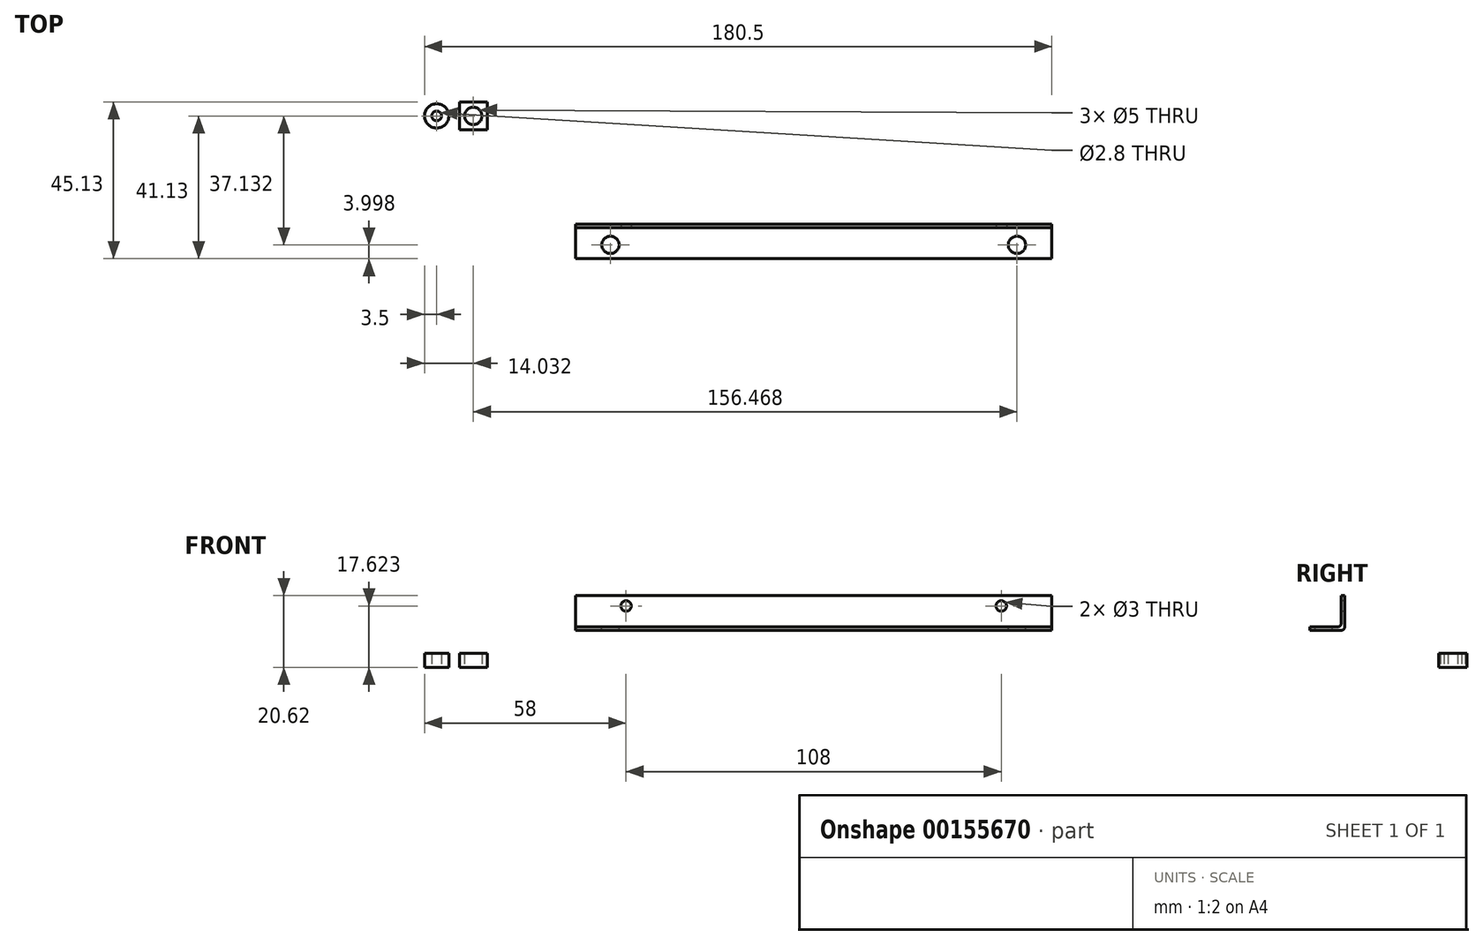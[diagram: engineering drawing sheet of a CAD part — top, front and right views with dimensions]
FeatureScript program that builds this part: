
annotation { "Feature Type Name" : "Feature", "Feature Type Description" : "" }
export const myFeature = defineFeature(function(context is Context, id is Id, definition is map)
    precondition{}
    {
        {
            var Q0;
            Q0=qCreatedBy(makeId("Right.planeOp"),FACE);
            var sketch = newSketch(context, id + "F0", { "sketchPlane" : qUnion([Q0])});
            skLineSegment(sketch, "E0.bottom", {"start": v(-31.13, 20.62) * mm, "end": v(-32.13, 20.62) * mm});
            skLineSegment(sketch, "E0.left", {"start": v(-31.13, 20.62) * mm, "end": v(-31.13, 10.62) * mm});
            skLineSegment(sketch, "E0.right", {"start": v(-32.13, 20.62) * mm, "end": v(-32.13, 11.62) * mm});
            skLineSegment(sketch, "E1.bottom", {"start": v(-31.13, 10.62) * mm, "end": v(-41.13, 10.62) * mm});
            skLineSegment(sketch, "E1.top", {"start": v(-32.13, 11.62) * mm, "end": v(-41.13, 11.62) * mm});
            skLineSegment(sketch, "E1.right", {"start": v(-41.13, 10.62) * mm, "end": v(-41.13, 11.62) * mm});
            skSolve(sketch);
        }
        {
            var Q0;
            Q0 = qSketchRegion(id + "F0", true);
            extrude(context, id + "F1", {"entities" : qUnion([Q0]), "depth" : 137 * mm});
        }
        {
            var Q0;
            Q0=makeQuery(id+"F1.opExtrude","SWEPT_FACE",FACE,{"disambiguationData":[OSD([sQuery(id+"F0.wireOp",EDGE,"E0.right")])]});
            var sketch = newSketch(context, id + "F2", { "sketchPlane" : qUnion([Q0])});
            skCircle(sketch, "E2", {"center": v(14.5, 17.62) * mm, "radius": 1.5 * mm});
            skCircle(sketch, "E3", {"center": v(122.5, 17.62) * mm, "radius": 1.5 * mm});
            skSolve(sketch);
        }
        {
            var Q0;
            Q0 = qSketchRegion(id + "F2", true);
            extrude(context, id + "F3", {"entities" : qUnion([Q0]), "operationType" : NewBodyOperationType.REMOVE, "oppositeDirection" : true, "depth" : 2 * mm});
        }
        {
            var Q0;
            Q0=makeQuery(id+"F1.opExtrude","SWEPT_FACE",FACE,{"disambiguationData":[OSD([sQuery(id+"F0.wireOp",EDGE,"E1.top")])]});
            var sketch = newSketch(context, id + "F4", { "sketchPlane" : qUnion([Q0])});
            skCircle(sketch, "E4", {"center": v(10, -37.13) * mm, "radius": 2.5 * mm});
            skCircle(sketch, "E5", {"center": v(127, -37.13) * mm, "radius": 2.5 * mm});
            skSolve(sketch);
        }
        {
            var Q0;
            Q0 = qSketchRegion(id + "F4", true);
            extrude(context, id + "F5", {"entities" : qUnion([Q0]), "operationType" : NewBodyOperationType.REMOVE, "oppositeDirection" : true, "depth" : 2 * mm});
        }
        {
            var Q0;
            Q0=makeQuery(id+"F1.opExtrude","SWEPT_EDGE",EDGE,{"disambiguationData":[OSD([sQuery(id+"F0.wireOp",EDGE,"E0.left"),sQuery(id+"F0.wireOp",EDGE,"E1.bottom")])]});
            var Q1;
            Q1=makeQuery(id+"F1.opExtrude","SWEPT_EDGE",EDGE,{"disambiguationData":[OSD([sQuery(id+"F0.wireOp",EDGE,"E0.right"),sQuery(id+"F0.wireOp",EDGE,"E1.top")])]});
            fillet(context, id + "F6", {"entities" : qUnion([Q0, Q1]), "radius" : 1 * mm, "tangentPropagation" : true, "allowEdgeOverflow" : false});
        }
        {
            var Q0;
            Q0=qCreatedBy(makeId("Top.planeOp"),FACE);
            var sketch = newSketch(context, id + "F7", { "sketchPlane" : qUnion([Q0])});
            skLineSegment(sketch, "E6.bottom", {"start": v(-25.47, -4) * mm, "end": v(-33.47, -4) * mm});
            skLineSegment(sketch, "E6.top", {"start": v(-25.47, 4) * mm, "end": v(-33.47, 4) * mm});
            skLineSegment(sketch, "E6.left", {"start": v(-25.47, -4) * mm, "end": v(-25.47, 4) * mm});
            skLineSegment(sketch, "E6.right", {"start": v(-33.47, -4) * mm, "end": v(-33.47, 4) * mm});
            skPoint(sketch, "E6.middle", {"position": v(-29.47, 0) * mm});
            skCircle(sketch, "E7", {"center": v(-29.47, 0) * mm, "radius": 2.5 * mm});
            skSolve(sketch);
        }
        {
            var Q0;
            Q0 = qSketchRegion(id + "F7", true);
            extrude(context, id + "F8", {"entities" : qUnion([Q0]), "depth" : 4 * mm});
        }
        {
            var Q0;
            Q0=qCreatedBy(makeId("Top.planeOp"),FACE);
            var sketch = newSketch(context, id + "F9", { "sketchPlane" : qUnion([Q0])});
            skCircle(sketch, "E8", {"center": v(-40, 0) * mm, "radius": 3.5 * mm});
            skCircle(sketch, "E9", {"center": v(-40, 0) * mm, "radius": 1.4 * mm});
            skSolve(sketch);
        }
        {
            var Q0;
            Q0 = qSketchRegion(id + "F9", true);
            extrude(context, id + "F10", {"entities" : qUnion([Q0]), "depth" : 4 * mm});
        }
    });
